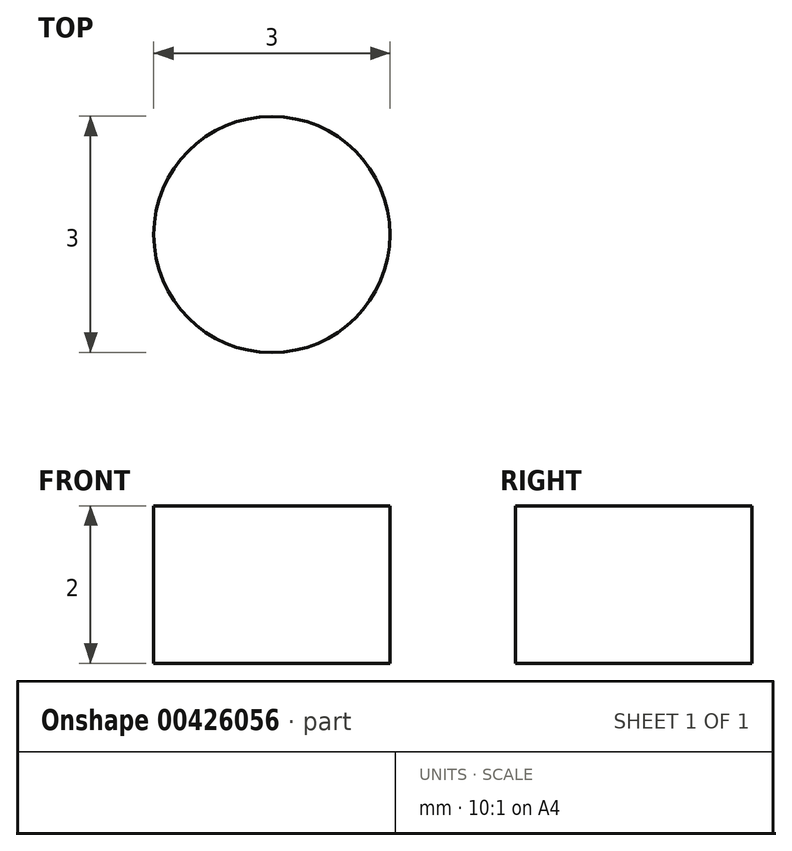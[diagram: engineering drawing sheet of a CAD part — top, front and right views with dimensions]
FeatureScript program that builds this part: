
annotation { "Feature Type Name" : "Feature", "Feature Type Description" : "" }
export const myFeature = defineFeature(function(context is Context, id is Id, definition is map)
    precondition{}
    {
        {
            var Q0;
            Q0=qCreatedBy(makeId("Top.planeOp"),FACE);
            var sketch = newSketch(context, id + "F0", { "sketchPlane" : qUnion([Q0])});
            skCircle(sketch, "E0.MirrorC", {"center": v(-22.01, 38.49) * mm, "radius": 1.5 * mm});
            skCircle(sketch, "E1.MirrorC", {"center": v(27.49, 38.49) * mm, "radius": 1.5 * mm});
            skCircle(sketch, "E2.MirrorC", {"center": v(22.74, -5.12) * mm, "radius": 1.5 * mm});
            skCircle(sketch, "E3.MirrorC", {"center": v(-17.26, -5.12) * mm, "radius": 1.5 * mm});
            skLineSegment(sketch, "E4.bottom", {"start": v(-38.8, 50.55) * mm, "end": v(38.8, 50.55) * mm});
            skLineSegment(sketch, "E4.top", {"start": v(-38.8, -69.74) * mm, "end": v(38.8, -69.74) * mm});
            skLineSegment(sketch, "E5", {"start": v(38.8, 50.55) * mm, "end": v(58.1, -9.6) * mm});
            skPoint(sketch, "E5.endSnap0", {"position": v(38.8, -9.6) * mm});
            skLineSegment(sketch, "E6", {"start": v(58.1, -9.6) * mm, "end": v(58.1, -69.74) * mm});
            skLineSegment(sketch, "E7", {"start": v(58.1, -69.74) * mm, "end": v(38.8, -69.74) * mm});
            skLineSegment(sketch, "E8.MirrorCS", {"start": v(-38.8, 50.55) * mm, "end": v(-58.1, -9.6) * mm});
            skLineSegment(sketch, "E9.MirrorCS", {"start": v(-58.1, -9.6) * mm, "end": v(-58.1, -69.74) * mm});
            skLineSegment(sketch, "E10.MirrorCS", {"start": v(-58.1, -69.74) * mm, "end": v(-38.8, -69.74) * mm});
            skSolve(sketch);
        }
        {
            var Q0;
            Q0=makeQuery(id+"F0.imprint","IMPRINT",FACE,{"disambiguationData":[TD([[makeQuery(id+"F0.imprint","IMPRINT",EDGE,{"derivedFrom":sQuery(id+"F0.wireOp",EDGE,"E0.MirrorC")}),1.0]])]});
            extrude(context, id + "F1", {"entities" : qUnion([Q0]), "depth" : 2 * mm});
        }
    });
